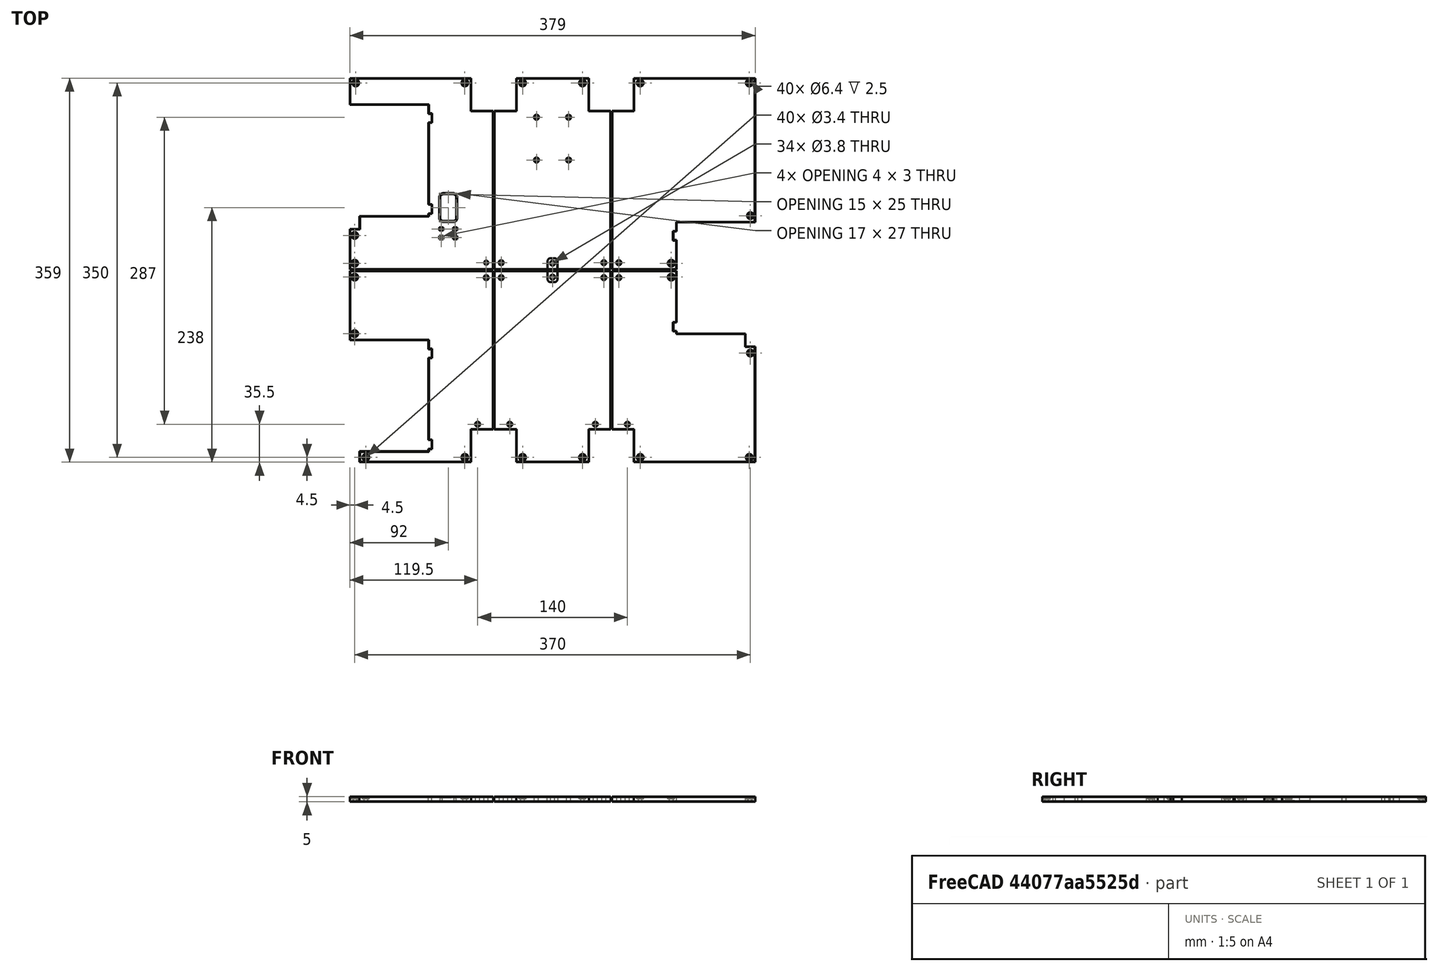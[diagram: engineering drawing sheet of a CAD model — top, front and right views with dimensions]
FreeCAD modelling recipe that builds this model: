
FCSTD DOCUMENT  (FreeCAD 0.19R24291 (Git))
Label: bottom-plate-250
License: Other
LicenseURL: GPL3
objects: Part::Feature×37, Part::Box×19, Part::MultiFuse×14, Part::Cylinder×12, Part::Cut×8, Part::Chamfer×7, Part::MultiCommon×6, Part::Fillet×1
note: 104 computed .brp shape members not serialized (recipe doc carries the construction recipe); baked Part::Feature solids carry a one-line shape summary decoded from their .brp

FEATURE [Part::Box] Box  label="Cube"
  AttacherType = Attacher::AttachEngine3D
  Height = 5
  Length = 379
  Placement = pos=(-189.5,-179.5,0) rot=(0,0,1;0rad)
  Width = 359
FEATURE [Part::Feature] Cut001003002001  label="motor-cut-slot"
  Placement = pos=(-190,-180,0) rot=(0,0,1;0rad)
  shape: bbox 77 x 116.1 x 10 mm, 16 faces (baked)
FEATURE [Part::Feature] Cut001003002002  label="motor-cut-slot001"
  Placement = pos=(-190,40,0) rot=(0,0,1;0rad)
  shape: bbox 77 x 116.1 x 10 mm, 16 faces (baked)
FEATURE [Part::Feature] Part__Mirroring002  label="motor-cut-slot002 (Mirror #1)001"
  Placement = pos=(0,110,0) rot=(0,0,1;0rad)
  shape: bbox 77 x 116.1 x 10 mm, 16 faces (baked)
FEATURE [Part::MultiFuse] Fusion
  Shapes = -> [Cut001003002001,Cut001003002002,Part__Mirroring002]
FEATURE [Part::Cut] Cut
  Base = -> Box
  Tool = -> Fusion
FEATURE [Part::Box] Box005  label="end-cut"
  AttacherType = Attacher::AttachEngine3D
  Height = 10
  Length = 42
  Placement = pos=(-76,-180,0) rot=(0,0,1;0rad)
  Width = 31
FEATURE [Part::Box] Box006  label="end-cut001"
  AttacherType = Attacher::AttachEngine3D
  Height = 10
  Length = 42
  Placement = pos=(34,-180,0) rot=(0,0,1;0rad)
  Width = 31
FEATURE [Part::Box] Box007  label="end-cut002"
  AttacherType = Attacher::AttachEngine3D
  Height = 10
  Length = 42
  Placement = pos=(34,149,0) rot=(0,0,1;0rad)
  Width = 31
FEATURE [Part::Box] Box008  label="end-cut003"
  AttacherType = Attacher::AttachEngine3D
  Height = 10
  Length = 42
  Placement = pos=(-76,149,0) rot=(0,0,1;0rad)
  Width = 31
FEATURE [Part::MultiFuse] Fusion001
  Shapes = -> [Box008,Box005,Box006,Box007]
FEATURE [Part::Cut] Cut001003002003
  Base = -> Cut
  Tool = -> Fusion001
FEATURE [Part::Cylinder] Cylinder
  Angle = 360
  AttacherType = Attacher::AttachEngine3D
  Height = 10
  Placement = pos=(-70,-144,0) rot=(0,0,1;0rad)
  Radius = 1.9
FEATURE [Part::Cylinder] Cylinder001
  Angle = 360
  AttacherType = Attacher::AttachEngine3D
  Height = 10
  Placement = pos=(70,-144,0) rot=(0,0,1;0rad)
  Radius = 1.9
FEATURE [Part::Cylinder] Cylinder002
  Angle = 360
  AttacherType = Attacher::AttachEngine3D
  Height = 10
  Placement = pos=(-40,-144,0) rot=(0,0,1;0rad)
  Radius = 1.9
FEATURE [Part::Cylinder] Cylinder003
  Angle = 360
  AttacherType = Attacher::AttachEngine3D
  Height = 10
  Placement = pos=(40,-144,0) rot=(0,0,1;0rad)
  Radius = 1.9
FEATURE [Part::MultiFuse] Fusion002
  Shapes = -> [Cylinder003,Cylinder,Cylinder001,Cylinder002]
FEATURE [Part::Cut] Cut001003002004
  Base = -> Cut001003002003
  Tool = -> Fusion002
FEATURE [Part::Cylinder] Cylinder004
  Angle = 360
  AttacherType = Attacher::AttachEngine3D
  Height = 10
  Placement = pos=(-15,143,0) rot=(0,0,1;0rad)
  Radius = 1.9
FEATURE [Part::Cylinder] Cylinder005
  Angle = 360
  AttacherType = Attacher::AttachEngine3D
  Height = 10
  Placement = pos=(15,143,0) rot=(0,0,1;0rad)
  Radius = 1.9
FEATURE [Part::Cylinder] Cylinder006
  Angle = 360
  AttacherType = Attacher::AttachEngine3D
  Height = 10
  Placement = pos=(15,103,0) rot=(0,0,1;0rad)
  Radius = 1.9
FEATURE [Part::Cylinder] Cylinder007
  Angle = 360
  AttacherType = Attacher::AttachEngine3D
  Height = 10
  Placement = pos=(-15,103,0) rot=(0,0,1;0rad)
  Radius = 1.9
FEATURE [Part::MultiFuse] Fusion003
  Shapes = -> [Cylinder004,Cylinder005,Cylinder006,Cylinder007]
FEATURE [Part::Cut] Cut001003002005
  Base = -> Cut001003002004
  Tool = -> Fusion003
FEATURE [Part::Box] Box009  label="Cube001"
  AttacherType = Attacher::AttachEngine3D
  Height = 10
  Length = 1
  Placement = pos=(-55.5,-180,0) rot=(0,0,1;0rad)
  Width = 360
FEATURE [Part::Box] Box010  label="Cube002"
  AttacherType = Attacher::AttachEngine3D
  Height = 10
  Length = 1
  Placement = pos=(54.5,-180,0) rot=(0,0,1;0rad)
  Width = 360
FEATURE [Part::Box] Box011  label="Cube003"
  AttacherType = Attacher::AttachEngine3D
  Height = 10
  Length = 380
  Placement = pos=(-190,-0.5,0) rot=(0,0,1;0rad)
  Width = 1
FEATURE [Part::MultiFuse] Fusion004  label="serepator"
  Shapes = -> [Box009,Box010,Box011]
FEATURE [Part::Cylinder] Cylinder008
  Angle = 360
  AttacherType = Attacher::AttachEngine3D
  Height = 10
  Placement = pos=(-7,7,0) rot=(0,0,1;0rad)
  Radius = 1.9
FEATURE [Part::Cylinder] Cylinder009
  Angle = 360
  AttacherType = Attacher::AttachEngine3D
  Height = 10
  Placement = pos=(7,7,0) rot=(0,0,1;0rad)
  Radius = 1.9
FEATURE [Part::Cylinder] Cylinder010
  Angle = 360
  AttacherType = Attacher::AttachEngine3D
  Height = 10
  Placement = pos=(-7,-7,0) rot=(0,0,1;0rad)
  Radius = 1.9
FEATURE [Part::Cylinder] Cylinder011
  Angle = 360
  AttacherType = Attacher::AttachEngine3D
  Height = 10
  Placement = pos=(7,-7,0) rot=(0,0,1;0rad)
  Radius = 1.9
FEATURE [Part::MultiFuse] Fusion005
  Placement = pos=(-55,0,0) rot=(0,0,1;0rad)
  Shapes = -> [Cylinder011,Cylinder008,Cylinder009,Cylinder010]
FEATURE [Part::Feature] Fusion005001
  Placement = pos=(55,0,0) rot=(0,0,1;0rad)
  shape: bbox 17.8 x 17.8 x 10 mm, 12 faces, 4 solids (baked)
FEATURE [Part::MultiFuse] Fusion005002
  Shapes = -> [Fusion005001,Fusion005]
FEATURE [Part::Cut] Cut001003002006
  Base = -> Cut001003002005
  Tool = -> Fusion005002
FEATURE [Part::Feature] Fusion005007  label="bolt-slot_U001"
  Placement = pos=(-184,175,0) rot=(0,0,1;0rad)
  shape: bbox 6.4 x 6.4 x 6 mm, 7 faces (baked)
FEATURE [Part::Feature] Fusion005008  label="bolt-slot_U002"
  Placement = pos=(184,175,0) rot=(0,0,1;0rad)
  shape: bbox 6.4 x 6.4 x 6 mm, 7 faces (baked)
FEATURE [Part::Feature] Fusion005009  label="bolt-slot_U003"
  Placement = pos=(-82,175,0) rot=(0,0,1;0rad)
  shape: bbox 6.4 x 6.4 x 6 mm, 7 faces (baked)
FEATURE [Part::Feature] Fusion005010  label="bolt-slot_U004"
  Placement = pos=(82,175,0) rot=(0,0,1;0rad)
  shape: bbox 6.4 x 6.4 x 6 mm, 7 faces (baked)
FEATURE [Part::Feature] Fusion005011  label="bolt-slot_U005"
  Placement = pos=(-28,175,0) rot=(0,0,1;0rad)
  shape: bbox 6.4 x 6.4 x 6 mm, 7 faces (baked)
FEATURE [Part::Feature] Fusion005012  label="bolt-slot_U006"
  Placement = pos=(28,175,0) rot=(0,0,1;0rad)
  shape: bbox 6.4 x 6.4 x 6 mm, 7 faces (baked)
FEATURE [Part::MultiFuse] Fusion005013
  Shapes = -> [Fusion005012,Fusion005008,Fusion005009,Fusion005010,Fusion005011,Fusion005007]
FEATURE [Part::Feature] Fusion005014  label="bolt-slot_D001"
  Placement = pos=(-174.5,-175,0) rot=(0,0,1;0rad)
  shape: bbox 6.4 x 6.4 x 6 mm, 7 faces (baked)
FEATURE [Part::Feature] Fusion005015  label="bolt-slot_D002"
  Placement = pos=(184,-175,0) rot=(0,0,1;0rad)
  shape: bbox 6.4 x 6.4 x 6 mm, 7 faces (baked)
FEATURE [Part::Feature] Fusion005016  label="bolt-slot_D003"
  Placement = pos=(-82,-175,0) rot=(0,0,1;0rad)
  shape: bbox 6.4 x 6.4 x 6 mm, 7 faces (baked)
FEATURE [Part::Feature] Fusion005017  label="bolt-slot_D004"
  Placement = pos=(82,-175,0) rot=(0,0,1;0rad)
  shape: bbox 6.4 x 6.4 x 6 mm, 7 faces (baked)
FEATURE [Part::Feature] Fusion005018  label="bolt-slot_D005"
  Placement = pos=(-28,-175,0) rot=(0,0,1;0rad)
  shape: bbox 6.4 x 6.4 x 6 mm, 7 faces (baked)
FEATURE [Part::Feature] Fusion005019  label="bolt-slot_D006"
  Placement = pos=(28,-175,0) rot=(0,0,1;0rad)
  shape: bbox 6.4 x 6.4 x 6 mm, 7 faces (baked)
FEATURE [Part::MultiFuse] Fusion005020
  Shapes = -> [Fusion005014,Fusion005015,Fusion005016,Fusion005017,Fusion005018,Fusion005019]
FEATURE [Part::Feature] Fusion005021  label="bolt-slot_L001"
  Placement = pos=(-185,6.5,0) rot=(0,0,1;0rad)
  shape: bbox 6.4 x 6.4 x 6 mm, 7 faces (baked)
FEATURE [Part::Feature] Fusion005022  label="bolt-slot_L002"
  Placement = pos=(-185,-6.5,0) rot=(0,0,1;0rad)
  shape: bbox 6.4 x 6.4 x 6 mm, 7 faces (baked)
FEATURE [Part::Feature] Fusion005023  label="bolt-slot_L003"
  Placement = pos=(-185,-59.36,0) rot=(0,0,1;0rad)
  shape: bbox 6.4 x 6.4 x 6 mm, 7 faces (baked)
FEATURE [Part::Feature] Fusion005024  label="bolt-slot_L004"
  Placement = pos=(-185,32.5,0) rot=(0,0,1;0rad)
  shape: bbox 6.4 x 6.4 x 6 mm, 7 faces (baked)
FEATURE [Part::MultiFuse] Fusion005025
  Shapes = -> [Fusion005024,Fusion005021,Fusion005022,Fusion005023]
FEATURE [Part::Feature] Fusion005026  label="bolt-slot_R001"
  Placement = pos=(185,50.94,0) rot=(0,0,1;0rad)
  shape: bbox 6.4 x 6.4 x 6 mm, 7 faces (baked)
FEATURE [Part::Feature] Fusion005027  label="bolt-slot_R002"
  Placement = pos=(185,-77.5,0) rot=(0,0,1;0rad)
  shape: bbox 6.4 x 6.4 x 6 mm, 7 faces (baked)
FEATURE [Part::MultiFuse] Fusion005028
  Shapes = -> [Fusion005027,Fusion005026]
FEATURE [Part::Box] Box012  label="Cube004"
  AttacherType = Attacher::AttachEngine3D
  Height = 10
  Length = 135
  Placement = pos=(-190,0,0) rot=(0,0,1;0rad)
  Width = 180
FEATURE [Part::Box] Box013  label="Cube005"
  AttacherType = Attacher::AttachEngine3D
  Height = 10
  Length = 135
  Placement = pos=(55,0,0) rot=(0,0,1;0rad)
  Width = 180
FEATURE [Part::Box] Box014  label="Cube006"
  AttacherType = Attacher::AttachEngine3D
  Height = 10
  Length = 135
  Placement = pos=(55,-180,0) rot=(0,0,1;0rad)
  Width = 180
FEATURE [Part::Box] Box015  label="Cube007"
  AttacherType = Attacher::AttachEngine3D
  Height = 10
  Length = 135
  Placement = pos=(-190,-180,0) rot=(0,0,1;0rad)
  Width = 180
FEATURE [Part::Box] Box016  label="Cube008"
  AttacherType = Attacher::AttachEngine3D
  Height = 10
  Length = 110
  Placement = pos=(-55,0,0) rot=(0,0,1;0rad)
  Width = 180
FEATURE [Part::Box] Box017  label="Cube009"
  AttacherType = Attacher::AttachEngine3D
  Height = 10
  Length = 110
  Placement = pos=(-55,-180,0) rot=(0,0,1;0rad)
  Width = 180
FEATURE [Part::Box] Box018  label="Cube010"
  AttacherType = Attacher::AttachEngine3D
  Height = 10
  Length = 15
  Placement = pos=(-105,46,0) rot=(0,0,1;0rad)
  Width = 25
FEATURE [Part::Box] Box019  label="Cube011"
  AttacherType = Attacher::AttachEngine3D
  Height = 10
  Length = 2
  Placement = pos=(-105,37,0) rot=(0,0,1;0rad)
  Width = 3
FEATURE [Part::Box] Box020  label="Cube012"
  AttacherType = Attacher::AttachEngine3D
  Height = 10
  Length = 2
  Placement = pos=(-105,29,0) rot=(0,0,1;0rad)
  Width = 3
FEATURE [Part::Box] Box021  label="Cube013"
  AttacherType = Attacher::AttachEngine3D
  Height = 10
  Length = 2
  Placement = pos=(-92,29,0) rot=(0,0,1;0rad)
  Width = 3
FEATURE [Part::Box] Box022  label="Cube014"
  AttacherType = Attacher::AttachEngine3D
  Height = 10
  Length = 2
  Placement = pos=(-92,37,0) rot=(0,0,1;0rad)
  Width = 3
FEATURE [Part::Fillet] Fillet
  Base = -> Box018
  Edges = 4 edges r=3: [Edge1,Edge3,Edge5,Edge7]
FEATURE [Part::MultiFuse] Fusion005030
  Shapes = -> [Box019,Box020,Box021,Box022,Fillet]
FEATURE [Part::Feature] Fusion005030004  label="bolt-slot"
  Placement = pos=(111,6.5,0) rot=(0,0,1;0rad)
  shape: bbox 6.4 x 6.4 x 6 mm, 7 faces (baked)
FEATURE [Part::Feature] Fusion005030005  label="bolt-slot001"
  Placement = pos=(111,-6.5,0) rot=(0,0,1;0rad)
  shape: bbox 6.4 x 6.4 x 6 mm, 7 faces (baked)
FEATURE [Part::MultiFuse] Fusion005030006
  Shapes = -> [Fusion005030005,Fusion005030004]
FEATURE [Part::MultiFuse] Fusion005030007
  Shapes = -> [Fusion005030006,Fusion005028,Fusion005025,Fusion005020,Fusion005013]
FEATURE [Part::Cut] Cut001003002007
  Base = -> Cut001003002006
  Tool = -> Fusion005030
FEATURE [Part::Cut] Cut001003002008
  Base = -> Cut001003002007
  Tool = -> Fusion005030007
FEATURE [Part::Cut] Cut001003002009  label="panel-combined"
  Base = -> Cut001003002008
  Tool = -> Fusion004
FEATURE [Part::Feature] Cut001003002009001  label="panel-combined001"
  shape: bbox 379 x 359 x 5 mm, 192 faces, 6 solids (baked)
FEATURE [Part::Feature] Cut001003002009002  label="panel-combined002"
  shape: bbox 379 x 359 x 5 mm, 192 faces, 6 solids (baked)
FEATURE [Part::Feature] Cut001003002009003  label="panel-combined003"
  shape: bbox 379 x 359 x 5 mm, 192 faces, 6 solids (baked)
FEATURE [Part::Feature] Cut001003002009004  label="panel-combined004"
  shape: bbox 379 x 359 x 5 mm, 192 faces, 6 solids (baked)
FEATURE [Part::Feature] Cut001003002009005  label="panel-combined005"
  shape: bbox 379 x 359 x 5 mm, 192 faces, 6 solids (baked)
FEATURE [Part::Feature] Cut001003002009006  label="panel-combined006"
  shape: bbox 379 x 359 x 5 mm, 192 faces, 6 solids (baked)
FEATURE [Part::MultiCommon] Common
  Shapes = -> [Box017,Cut001003002009001]
FEATURE [Part::MultiCommon] Common001
  Shapes = -> [Box016,Cut001003002009002]
FEATURE [Part::MultiCommon] Common002
  Shapes = -> [Box015,Cut001003002009003]
FEATURE [Part::MultiCommon] Common003
  Shapes = -> [Box014,Cut001003002009004]
FEATURE [Part::MultiCommon] Common004
  Shapes = -> [Box013,Cut001003002009005]
FEATURE [Part::MultiCommon] Common005
  Shapes = -> [Box012,Cut001003002009006]
FEATURE [Part::Chamfer] Chamfer
  Base = -> Common005
  Edges = 40 edges r=0.4: [Edge1,Edge3,Edge5,Edge6,Edge7,Edge8,Edge9,Edge10,Edge11,Edge12,Edge13,Edge14,Edge15,Edge16,Edge17,Edge18,Edge19,Edge20,Edge21,Edge22,Edge23,Edge53,Edge55,Edge56,Edge57,Edge58,Edge59,Edge60,Edge61,Edge62,Edge63,Edge64,Edge65,Edge66,Edge67,Edge68,Edge69,Edge70,Edge71,Edge72]
FEATURE [Part::Chamfer] Chamfer001
  Base = -> Chamfer
  Edges = 32 edges r=1: [Edge45,Edge47,Edge49,Edge51,Edge53,Edge54,Edge55,Edge56,Edge57,Edge58,Edge59,Edge60,Edge62,Edge64,Edge66,Edge68,Edge94,Edge96,Edge98,Edge100,Edge101,Edge102,Edge103,Edge104,Edge105,Edge106,Edge107,Edge108,Edge111,Edge113,Edge115,Edge117]
FEATURE [Part::Chamfer] Chamfer002
  Base = -> Common002
  Edges = 44 edges r=0.4: [Edge1,Edge3,Edge5,Edge6,Edge7,Edge8,Edge9,Edge10,Edge11,Edge12,Edge13,Edge14,Edge15,Edge16,Edge17,Edge18,Edge19,Edge20,Edge21,Edge24,Edge27,Edge28,Edge30,Edge31,Edge32,Edge33,Edge34,Edge35,Edge36,Edge37,Edge38,Edge39,Edge40,Edge41,Edge42,Edge43,Edge44,Edge45,Edge46,Edge47,Edge48,Edge49,Edge50,+1 more]
FEATURE [Part::Chamfer] Chamfer003
  Base = -> Common
  Edges = 26 edges r=0.4: [Edge1,Edge2,Edge3,Edge4,Edge5,Edge6,Edge7,Edge8,Edge10,Edge11,Edge13,Edge14,Edge16,Edge18,Edge20,Edge23,Edge25,Edge26,Edge29,Edge30,Edge34,Edge36,Edge40,Edge42,Edge43,Edge44]
FEATURE [Part::Chamfer] Chamfer004
  Base = -> Common003
  Edges = 36 edges r=0.4: [Edge1,Edge2,Edge3,Edge4,Edge5,Edge6,Edge7,Edge8,Edge9,Edge10,Edge11,Edge12,Edge13,Edge14,Edge16,Edge18,Edge22,Edge24,Edge26,Edge29,Edge31,Edge33,Edge34,Edge36,Edge39,Edge40,Edge42,Edge44,Edge47,Edge48,Edge52,Edge56,Edge61,Edge62,Edge63,Edge64]
FEATURE [Part::Chamfer] Chamfer005
  Base = -> Common004
  Edges = 30 edges r=0.4: [Edge1,Edge2,Edge3,Edge4,Edge5,Edge6,Edge7,Edge8,Edge9,Edge10,Edge11,Edge12,Edge13,Edge20,Edge22,Edge23,Edge25,Edge27,Edge29,Edge32,Edge34,Edge36,Edge37,Edge39,Edge41,Edge43,Edge52,Edge53,Edge54,Edge55]
FEATURE [Part::Chamfer] Chamfer006
  Base = -> Common001
  Edges = 30 edges r=0.4: [Edge1,Edge2,Edge3,Edge4,Edge5,Edge6,Edge7,Edge8,Edge9,Edge10,Edge11,Edge13,Edge14,Edge15,Edge19,Edge21,Edge22,Edge25,Edge27,Edge28,Edge30,Edge32,Edge34,Edge36,Edge38,Edge42,Edge44,Edge46,Edge49,Edge50]
FEATURE [Part::Feature] Chamfer007  label="panel-side-connector"
  shape: bbox 10 x 23 x 5 mm, 32 faces (baked)
FEATURE [Part::Feature] Chamfer001001
  shape: bbox 134 x 179 x 5 mm, 131 faces (baked)
FEATURE [Part::Feature] Chamfer002001
  shape: bbox 134 x 179 x 5 mm, 78 faces (baked)
FEATURE [Part::Feature] Chamfer003001
  shape: bbox 109 x 179 x 5 mm, 46 faces (baked)
FEATURE [Part::Feature] Chamfer004001
  shape: bbox 134 x 179 x 5 mm, 66 faces (baked)
FEATURE [Part::Feature] Chamfer005001
  shape: bbox 134 x 179 x 5 mm, 57 faces (baked)
FEATURE [Part::Feature] Chamfer006001
  shape: bbox 109 x 179 x 5 mm, 52 faces (baked)
